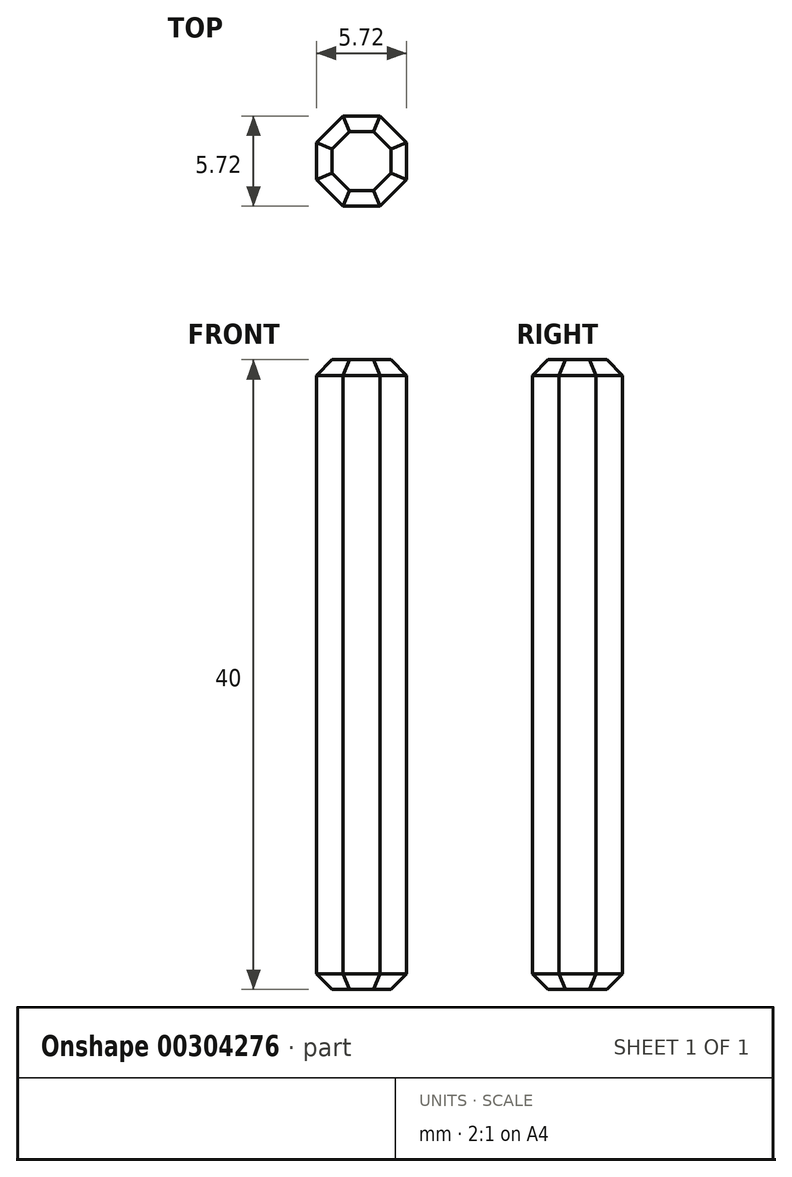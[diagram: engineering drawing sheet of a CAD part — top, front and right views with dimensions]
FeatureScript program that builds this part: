
annotation { "Feature Type Name" : "Feature", "Feature Type Description" : "" }
export const myFeature = defineFeature(function(context is Context, id is Id, definition is map)
    precondition{}
    {
        {
            var Q0;
            Q0=qCreatedBy(makeId("Top.planeOp"),FACE);
            var sketch = newSketch(context, id + "F0", { "sketchPlane" : qUnion([Q0])});
            skCircle(sketch, "E0", {"center": v(0, 0) * mm, "radius": 2.86 * mm, "construction": true});
            skCircle(sketch, "E1.cCircle", {"center": v(0, 0) * mm, "radius": 3.1 * mm, "construction": true});
            skLineSegment(sketch, "E1.0", {"start": v(2.86, 1.19) * mm, "end": v(2.86, -1.19) * mm});
            skLineSegment(sketch, "E1.1", {"start": v(2.86, -1.19) * mm, "end": v(1.19, -2.86) * mm});
            skLineSegment(sketch, "E1.2", {"start": v(1.19, -2.86) * mm, "end": v(-1.19, -2.86) * mm});
            skLineSegment(sketch, "E1.3", {"start": v(-1.19, -2.86) * mm, "end": v(-2.86, -1.19) * mm});
            skLineSegment(sketch, "E1.4", {"start": v(-2.86, -1.19) * mm, "end": v(-2.86, 1.19) * mm});
            skLineSegment(sketch, "E1.5", {"start": v(-2.86, 1.19) * mm, "end": v(-1.19, 2.86) * mm});
            skLineSegment(sketch, "E1.6", {"start": v(-1.19, 2.86) * mm, "end": v(1.19, 2.86) * mm});
            skLineSegment(sketch, "E1.7", {"start": v(1.19, 2.86) * mm, "end": v(2.86, 1.19) * mm});
            skCircle(sketch, "E2", {"center": v(0, 0) * mm, "radius": 2.98 * mm, "construction": true});
            skSolve(sketch);
        }
        {
            var Q0;
            Q0 = qSketchRegion(id + "F0", true);
            extrude(context, id + "F1", {"entities" : qUnion([Q0]), "depth" : 40 * mm});
        }
        {
            var Q0;
            Q0=makeQuery(id+"F1.opExtrude","CAP_FACE",FACE,{"disambiguationData":[OSD([sQuery(id+"F0.wireOp",EDGE,"E1.0"),sQuery(id+"F0.wireOp",EDGE,"E1.1"),sQuery(id+"F0.wireOp",EDGE,"E1.2"),sQuery(id+"F0.wireOp",EDGE,"E1.3"),sQuery(id+"F0.wireOp",EDGE,"E1.4"),sQuery(id+"F0.wireOp",EDGE,"E1.5"),sQuery(id+"F0.wireOp",EDGE,"E1.6"),sQuery(id+"F0.wireOp",EDGE,"E1.7")])],"isStart":false});
            var Q1;
            Q1=makeQuery(id+"F1.opExtrude","CAP_FACE",FACE,{"disambiguationData":[OSD([sQuery(id+"F0.wireOp",EDGE,"E1.0"),sQuery(id+"F0.wireOp",EDGE,"E1.1"),sQuery(id+"F0.wireOp",EDGE,"E1.2"),sQuery(id+"F0.wireOp",EDGE,"E1.3"),sQuery(id+"F0.wireOp",EDGE,"E1.4"),sQuery(id+"F0.wireOp",EDGE,"E1.5"),sQuery(id+"F0.wireOp",EDGE,"E1.6"),sQuery(id+"F0.wireOp",EDGE,"E1.7")])],"isStart":true});
            chamfer(context, id + "F2", {"entities" : qUnion([Q0, Q1]), "width" : 1 * mm, "tangentPropagation" : true});
        }
    });
